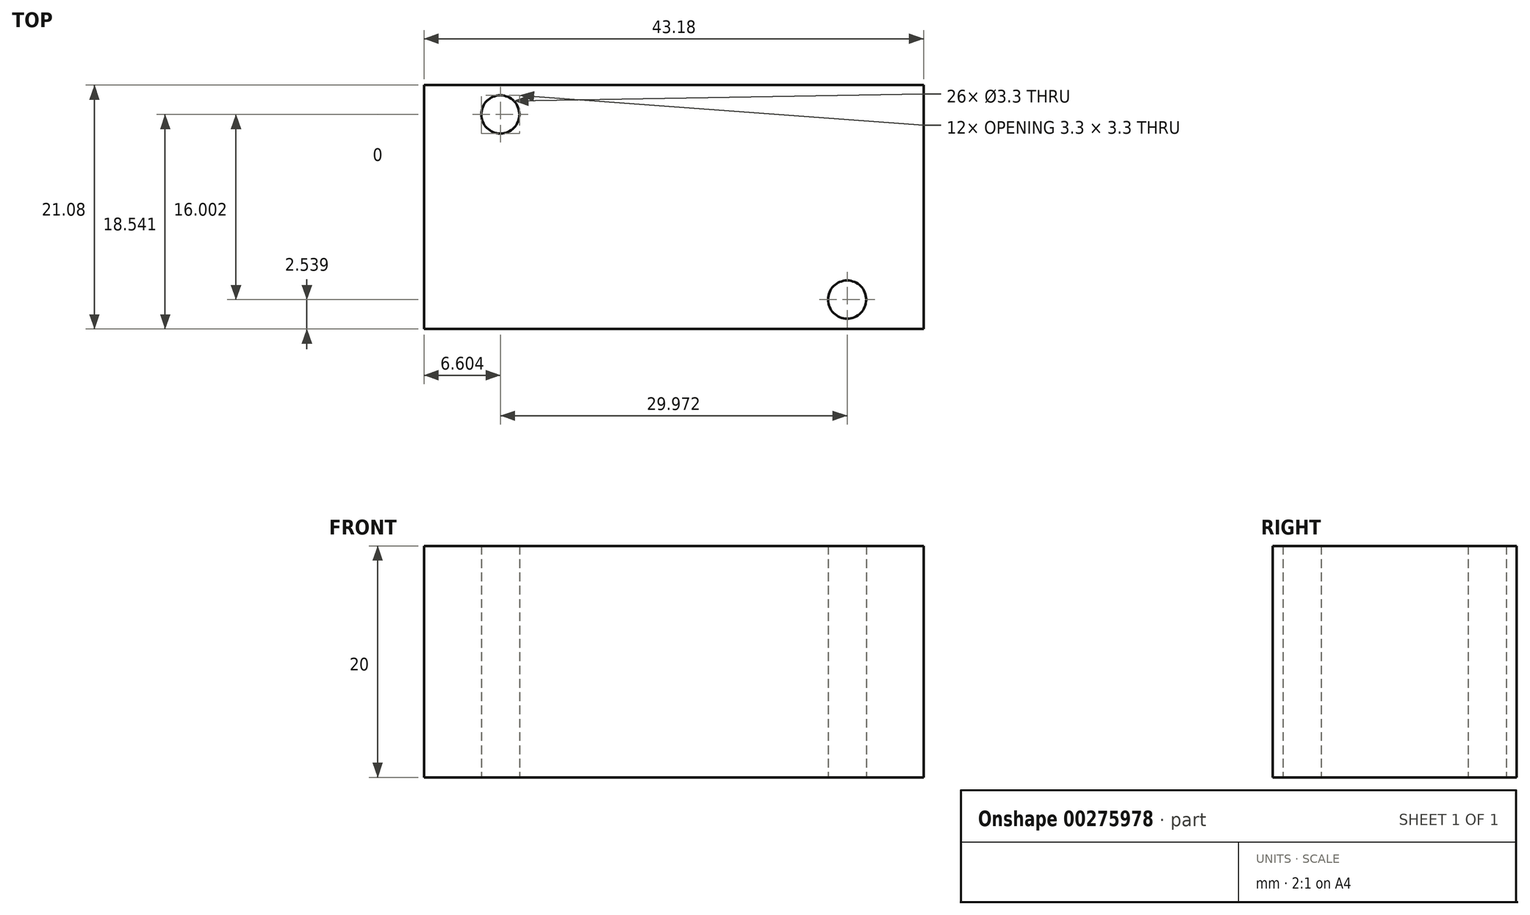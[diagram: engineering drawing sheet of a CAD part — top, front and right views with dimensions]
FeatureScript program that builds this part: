
annotation { "Feature Type Name" : "Feature", "Feature Type Description" : "" }
export const myFeature = defineFeature(function(context is Context, id is Id, definition is map)
    precondition{}
    {
        {
            var Q0;
            Q0=qCreatedBy(makeId("Top.planeOp"),FACE);
            var sketch = newSketch(context, id + "F0", { "sketchPlane" : qUnion([Q0])});
            skLineSegment(sketch, "E0.bottom", {"start": v(-21.6, 10.54) * mm, "end": v(21.6, 10.54) * mm});
            skLineSegment(sketch, "E0.top", {"start": v(-21.6, -10.54) * mm, "end": v(21.6, -10.54) * mm});
            skLineSegment(sketch, "E0.left", {"start": v(-21.59, 10.54) * mm, "end": v(-21.6, -10.54) * mm});
            skLineSegment(sketch, "E0.right", {"start": v(21.6, 10.54) * mm, "end": v(21.59, -10.54) * mm});
            skPoint(sketch, "E1", {"position": v(0, 10.54) * mm});
            skPoint(sketch, "E2", {"position": v(21.59, 0) * mm});
            skPoint(sketch, "E3", {"position": v(-14.99, 8) * mm});
            skPoint(sketch, "E4", {"position": v(14.99, -8) * mm});
            skSolve(sketch);
        }
        {
            var Q0;
            Q0=makeQuery(id+"F0.imprint","IMPRINT",FACE,{"disambiguationData":[TD([[makeQuery(id+"F0.imprint","IMPRINT",EDGE,{"derivedFrom":sQuery(id+"F0.wireOp",EDGE,"E0.bottom")}),-1.0]])]});
            extrude(context, id + "F1", {"entities" : qUnion([Q0]), "depth" : 20 * mm});
        }
        {
            var Q0;
            Q0=sQuery(id+"F0.wireOp",VERTEX,"E3");
            var Q1;
            Q1=sQuery(id+"F0.wireOp",VERTEX,"E4");
            var Q2;
            Q2=makeQuery(id+"F1.opExtrude","SWEPT_BODY",BODY,{"disambiguationData":[OSD([sQuery(id+"F0.wireOp",EDGE,"E0.bottom"),sQuery(id+"F0.wireOp",EDGE,"E0.top"),sQuery(id+"F0.wireOp",EDGE,"E0.left"),sQuery(id+"F0.wireOp",EDGE,"E0.right")])]});
            hole(context, id + "F2", {"style" : HoleStyle.SIMPLE, "endStyle" : HoleEndStyle.THROUGH, "oppositeDirection" : true, "standardTappedOrClearance" : lookupTablePath({ "standard" : "ISO", "fit" : "Normal", "size" : "M3", "type" : "Clearance" }), "standardBlindInLast" : lookupTablePath({ "fit" : "Standard", "standard" : "ISO", "size" : "M3", "type" : "Clearance" }), "holeDiameter" : 3.3 * mm, "tappedDepth" : 13.2 * mm, "tapClearance" : 3, "startFromSketch" : true, "locations" : qUnion([Q0, Q1]), "scope" : qUnion([Q2])});
        }
    });
